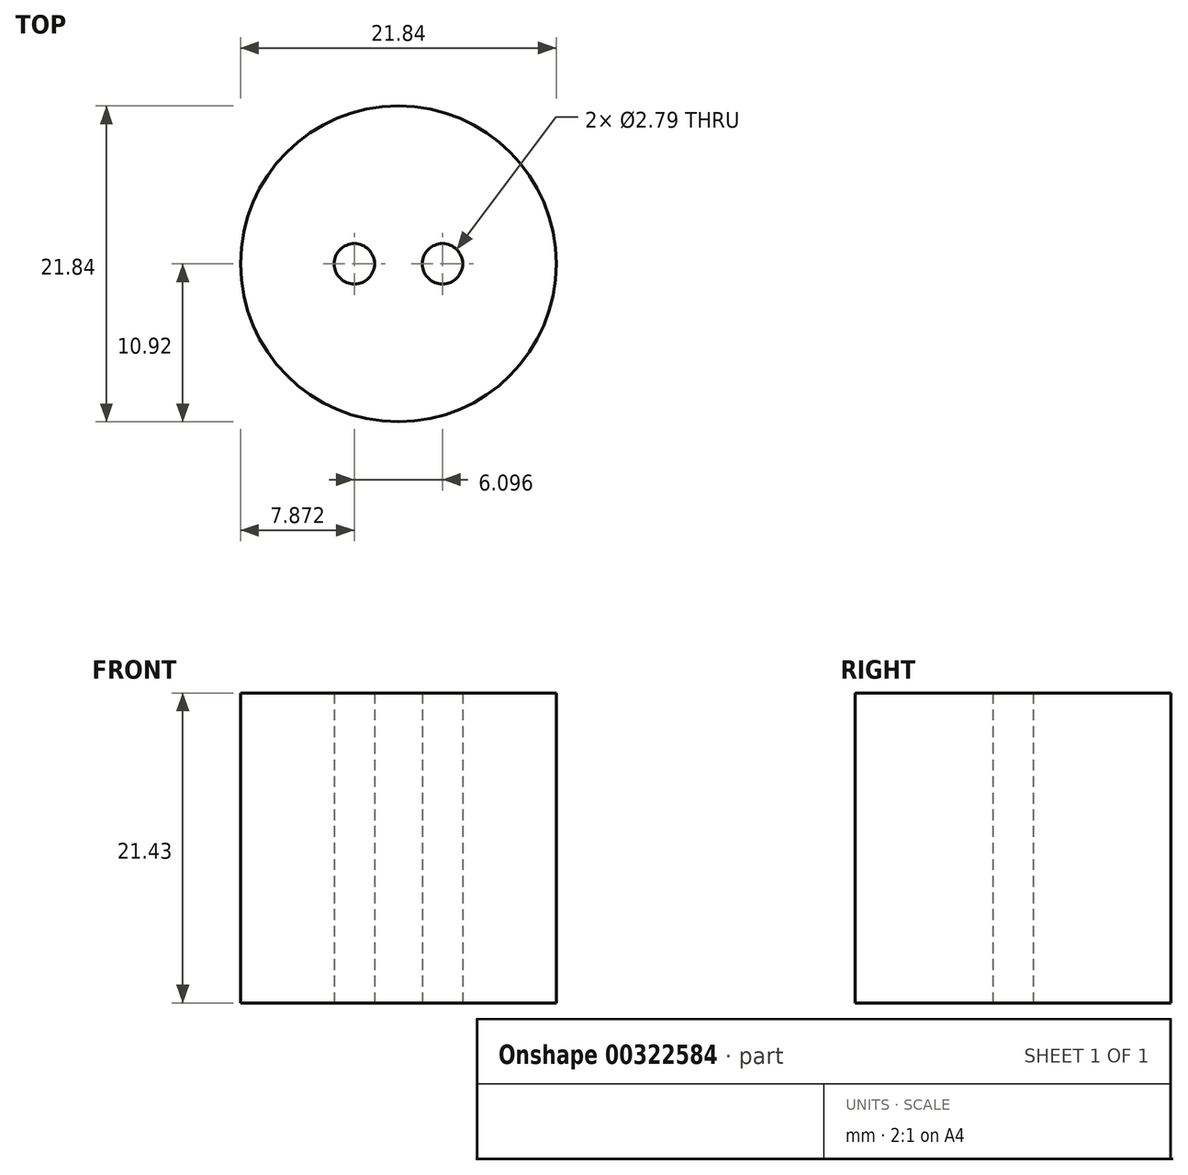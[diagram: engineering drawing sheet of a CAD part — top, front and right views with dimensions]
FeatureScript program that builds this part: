
annotation { "Feature Type Name" : "Feature", "Feature Type Description" : "" }
export const myFeature = defineFeature(function(context is Context, id is Id, definition is map)
    precondition{}
    {
        {
            var Q0;
            Q0=qCreatedBy(makeId("Top.planeOp"),FACE);
            var sketch = newSketch(context, id + "F0", { "sketchPlane" : qUnion([Q0])});
            skCircle(sketch, "E0", {"center": v(0, 0) * mm, "radius": 10.92 * mm});
            skCircle(sketch, "E1", {"center": v(-3.05, 0) * mm, "radius": 1.4 * mm});
            skCircle(sketch, "E2.MirrorC", {"center": v(3.05, 0) * mm, "radius": 1.4 * mm});
            skLineSegment(sketch, "E3", {"start": v(-10.92, 0) * mm, "end": v(10.92, 0) * mm, "construction": true});
            skSolve(sketch);
        }
        {
            var Q0;
            Q0=makeQuery(id+"F0.imprint","IMPRINT",FACE,{"disambiguationData":[TD([[makeQuery(id+"F0.imprint","IMPRINT",EDGE,{"derivedFrom":sQuery(id+"F0.wireOp",EDGE,"E0")}),1.0]])]});
            extrude(context, id + "F1", {"entities" : qUnion([Q0]), "depth" : 21.43 * mm, "offsetDistance" : 25.4 * mm});
        }
    });
